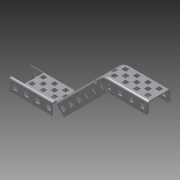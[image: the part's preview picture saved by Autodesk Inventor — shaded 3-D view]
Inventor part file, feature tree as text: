
AUTODESK INVENTOR PART (.ipt)
format: ipt  version: 2012 (Build 160160000, 160)  size: 2,351,616 bytes
history: native  units: in
note: dims shown in document units (in); Inventor stores cm internally (conversion verified against a paired STEP export)
features: sketch x11, extrude x4, other x3, plane x2, imported_body x1, split x1
ambient origin geometry x8: Origin, YZ Plane, XZ Plane, XY Plane, X Axis, Y Axis, Z Axis, Center Point
feature tree (22):
  parser-record x1  (decoder bookkeeping rows leaked as tree rows — omitted from the tree; the rows remain in map.json)
  imported_body  "Base1"
  sketch  "Sketch1"  dims[d0=1.0in d1=0.0in d4=0.2in d5=45.0deg]
  extrude  "Extrusion1"  Depth=0.2in TaperAngle=45.0deg
  sketch  "Sketch3"  dims[d6=-2.5in d7=0.5in d8=0.0in]
  sketch  "Sketch4"  dims[d17=0.125in d18=3.0in d19=0.0in]
  other  "Bend Part1"
  sketch  "Sketch5"  dims[d27=0.55in d28=45.0deg d30=0.0in]
  plane  "Work Plane1"
  extrude  "Extrusion3"  Depth=0.5in TaperAngle=0.0deg
  sketch  "Sketch8"
  sketch  "Sketch9"
  sketch  "Sketch10"
  extrude  "Extrusion6"  Depth=3.0in TaperAngle=0.0deg
  other  "Bend Part5"
  plane  "Work Plane2"
  split  "Split2"
  extrude  "Extrusion7"  TaperAngle=0.0deg  [1 undecoded]
  sketch  "Sketch6"  dims[d31=3.0in d32=0.0in]
  sketch  "Sketch11"
  sketch  "Sketch12"
  sketch  "Sketch13"
note: 1 required parameter value undecoded (feature->parameter linkage not recoverable at this tier; creation-order binding heuristic only, values carry confidence <= 0.55)
